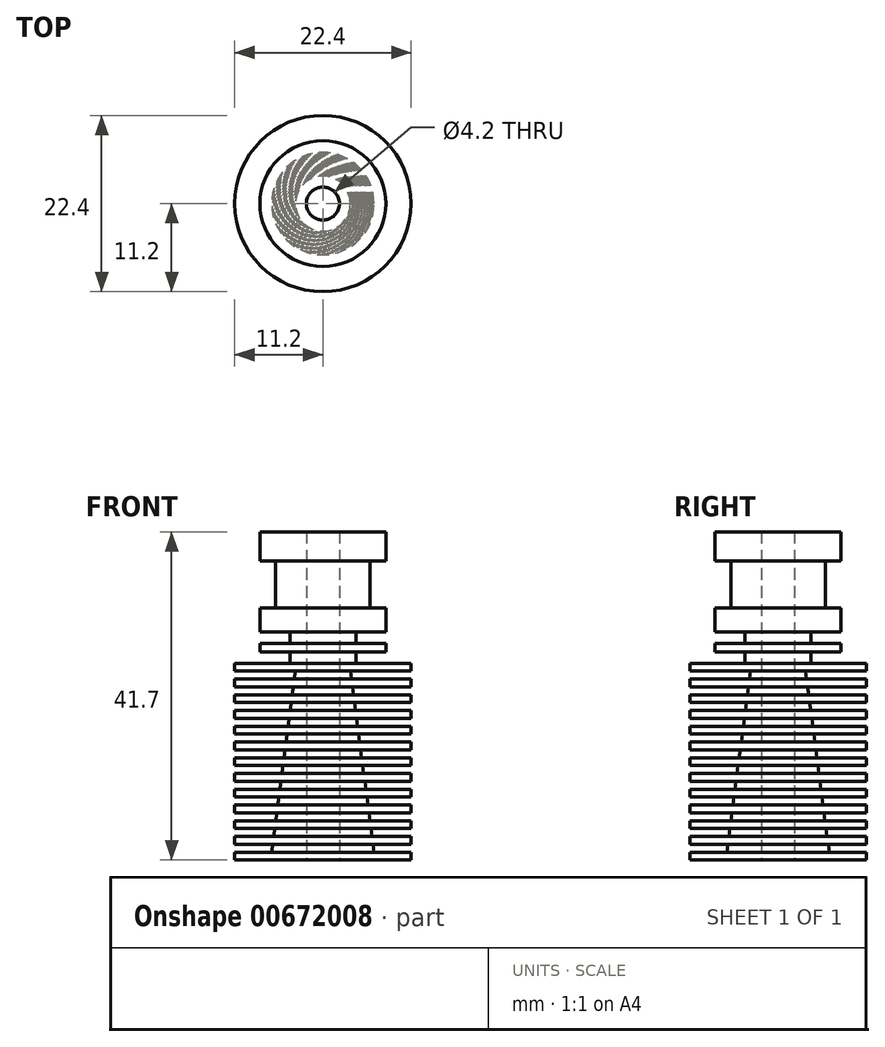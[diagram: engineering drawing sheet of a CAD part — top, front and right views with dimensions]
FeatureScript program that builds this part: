
annotation { "Feature Type Name" : "Feature", "Feature Type Description" : "" }
export const myFeature = defineFeature(function(context is Context, id is Id, definition is map)
    precondition{}
    {
        {
            var Q0;
            Q0=qCreatedBy(makeId("Front.planeOp"),FACE);
            var sketch = newSketch(context, id + "F0", { "sketchPlane" : qUnion([Q0])});
            skLineSegment(sketch, "E0", {"start": v(0, 0) * mm, "end": v(0, -46.74) * mm, "construction": true});
            skLineSegment(sketch, "E1", {"start": v(0, 0) * mm, "end": v(8, 0) * mm});
            skLineSegment(sketch, "E2", {"start": v(8, 0) * mm, "end": v(8, -3.7) * mm});
            skLineSegment(sketch, "E3", {"start": v(8, -3.7) * mm, "end": v(6, -3.7) * mm});
            skLineSegment(sketch, "E4", {"start": v(6, -3.7) * mm, "end": v(6, -9.7) * mm});
            skLineSegment(sketch, "E5", {"start": v(6, -9.7) * mm, "end": v(8, -9.7) * mm});
            skLineSegment(sketch, "E6", {"start": v(8, -9.7) * mm, "end": v(8, -12.7) * mm});
            skLineSegment(sketch, "E7", {"start": v(8, -12.7) * mm, "end": v(4.2, -12.7) * mm});
            skLineSegment(sketch, "E8", {"start": v(4.2, -12.7) * mm, "end": v(4.2, -14.15) * mm});
            skLineSegment(sketch, "E9", {"start": v(4.2, -14.15) * mm, "end": v(8, -14.15) * mm});
            skLineSegment(sketch, "E10", {"start": v(8, -14.15) * mm, "end": v(8, -15.24) * mm});
            skLineSegment(sketch, "E11", {"start": v(8, -15.24) * mm, "end": v(4.2, -15.24) * mm});
            skLineSegment(sketch, "E12", {"start": v(4.2, -15.24) * mm, "end": v(4.2, -16.7) * mm});
            skLineSegment(sketch, "E13", {"start": v(4.2, -16.7) * mm, "end": v(11.2, -16.7) * mm});
            skLineSegment(sketch, "E14", {"start": v(11.2, -16.7) * mm, "end": v(11.2, -41.7) * mm});
            skLineSegment(sketch, "E15", {"start": v(11.2, -41.7) * mm, "end": v(0, -41.7) * mm});
            skLineSegment(sketch, "E16", {"start": v(0, 0) * mm, "end": v(0, -41.7) * mm});
            skSolve(sketch);
        }
        {
            var Q0;
            Q0=makeQuery(id+"F0.imprint","IMPRINT",FACE,{"disambiguationData":[TD([[makeQuery(id+"F0.imprint","IMPRINT",EDGE,{"derivedFrom":sQuery(id+"F0.wireOp",EDGE,"E1")}),-1.0]])]});
            var Q1;
            Q1=sQuery(id+"F0.wireOp",EDGE,"E0");
            revolve(context, id + "F1", {"entities" : qUnion([Q0]), "axis" : qUnion([Q1]), "revolveType" : RevolveType.FULL});
        }
        {
            var Q0;
            Q0=makeQuery(id+"F1.opRevolve","SWEPT_FACE",FACE,{"disambiguationData":[OSD([sQuery(id+"F0.wireOp",EDGE,"E15")])]});
            var sketch = newSketch(context, id + "F2", { "sketchPlane" : qUnion([Q0])});
            skPoint(sketch, "E17", {"position": v(0, 0) * mm});
            skSolve(sketch);
        }
        {
            var Q0;
            Q0=sQuery(id+"F2.wireOp",VERTEX,"E17");
            var Q1;
            Q1=makeQuery(id+"F1.opRevolve","SWEPT_BODY",BODY,{"disambiguationData":[OSD([sQuery(id+"F0.wireOp",EDGE,"E1"),sQuery(id+"F0.wireOp",EDGE,"E2"),sQuery(id+"F0.wireOp",EDGE,"E3"),sQuery(id+"F0.wireOp",EDGE,"E4"),sQuery(id+"F0.wireOp",EDGE,"E5"),sQuery(id+"F0.wireOp",EDGE,"E6"),sQuery(id+"F0.wireOp",EDGE,"E7"),sQuery(id+"F0.wireOp",EDGE,"E8"),sQuery(id+"F0.wireOp",EDGE,"E9"),sQuery(id+"F0.wireOp",EDGE,"E10"),sQuery(id+"F0.wireOp",EDGE,"E11"),sQuery(id+"F0.wireOp",EDGE,"E12"),sQuery(id+"F0.wireOp",EDGE,"E13"),sQuery(id+"F0.wireOp",EDGE,"E14"),sQuery(id+"F0.wireOp",EDGE,"E15"),sQuery(id+"F0.wireOp",EDGE,"E16")])]});
            hole(context, id + "F3", {"style" : HoleStyle.SIMPLE, "endStyle" : HoleEndStyle.THROUGH, "standardTappedOrClearance" : lookupTablePath({ "standard" : "ISO", "engagement" : "75%", "pitch" : "0.8 mm", "size" : "M5", "type" : "Tapped" }), "standardBlindInLast" : lookupTablePath({ "standard" : "ISO", "engagement" : "75%", "pitch" : "0.8 mm", "size" : "M5", "type" : "Tapped" }), "holeDiameter" : 4.2 * mm, "majorDiameter" : 5 * mm, "showTappedDepth" : true, "isTappedThrough" : true, "tappedDepth" : 7.6 * mm, "tapClearance" : 3, "startFromSketch" : true, "locations" : qUnion([Q0]), "scope" : qUnion([Q1])});
        }
        {
            var Q0;
            Q0=qCreatedBy(makeId("Front.planeOp"),FACE);
            var sketch = newSketch(context, id + "F4", { "sketchPlane" : qUnion([Q0])});
            skLineSegment(sketch, "E18", {"start": v(0, -16.7) * mm, "end": v(11.2, -16.7) * mm});
            skLineSegment(sketch, "E19", {"start": v(11.2, -16.7) * mm, "end": v(11.2, -17.7) * mm});
            skLineSegment(sketch, "E20", {"start": v(11.2, -17.7) * mm, "end": v(3.5, -17.7) * mm});
            skLineSegment(sketch, "E21", {"start": v(3.63, -18.7) * mm, "end": v(11.2, -18.7) * mm});
            skLineSegment(sketch, "E22", {"start": v(11.2, -18.7) * mm, "end": v(11.2, -17.7) * mm});
            skLineSegment(sketch, "E23", {"start": v(0, -16.7) * mm, "end": v(0, -19.3) * mm});
            skLineSegment(sketch, "E24", {"start": v(11.2, -19.7) * mm, "end": v(3.76, -19.7) * mm});
            skLineSegment(sketch, "E25", {"start": v(3.9, -20.7) * mm, "end": v(11.2, -20.7) * mm});
            skLineSegment(sketch, "E26", {"start": v(11.2, -21.7) * mm, "end": v(4.02, -21.7) * mm});
            skLineSegment(sketch, "E27", {"start": v(4.15, -22.7) * mm, "end": v(11.2, -22.7) * mm});
            skLineSegment(sketch, "E28", {"start": v(11.2, -23.7) * mm, "end": v(4.28, -23.7) * mm});
            skLineSegment(sketch, "E29", {"start": v(4.41, -24.7) * mm, "end": v(11.2, -24.7) * mm});
            skLineSegment(sketch, "E30", {"start": v(11.2, -25.7) * mm, "end": v(4.54, -25.7) * mm});
            skLineSegment(sketch, "E31", {"start": v(4.67, -26.7) * mm, "end": v(11.2, -26.7) * mm});
            skLineSegment(sketch, "E32", {"start": v(11.2, -27.7) * mm, "end": v(4.8, -27.7) * mm});
            skLineSegment(sketch, "E33", {"start": v(4.93, -28.7) * mm, "end": v(11.2, -28.7) * mm});
            skLineSegment(sketch, "E34", {"start": v(11.2, -29.7) * mm, "end": v(5.07, -29.7) * mm});
            skLineSegment(sketch, "E35", {"start": v(5.2, -30.7) * mm, "end": v(11.2, -30.7) * mm});
            skLineSegment(sketch, "E36", {"start": v(11.2, -31.7) * mm, "end": v(5.33, -31.7) * mm});
            skLineSegment(sketch, "E37", {"start": v(5.46, -32.7) * mm, "end": v(11.2, -32.7) * mm});
            skLineSegment(sketch, "E38", {"start": v(11.2, -33.7) * mm, "end": v(5.59, -33.7) * mm});
            skLineSegment(sketch, "E39", {"start": v(5.72, -34.7) * mm, "end": v(11.2, -34.7) * mm});
            skLineSegment(sketch, "E40", {"start": v(11.2, -35.7) * mm, "end": v(5.85, -35.7) * mm});
            skLineSegment(sketch, "E41", {"start": v(5.98, -36.7) * mm, "end": v(11.2, -36.7) * mm});
            skLineSegment(sketch, "E42", {"start": v(11.2, -37.7) * mm, "end": v(6.1, -37.7) * mm});
            skLineSegment(sketch, "E43", {"start": v(6.24, -38.7) * mm, "end": v(11.2, -38.7) * mm});
            skLineSegment(sketch, "E44", {"start": v(11.2, -39.7) * mm, "end": v(6.37, -39.7) * mm});
            skLineSegment(sketch, "E45", {"start": v(6.5, -40.7) * mm, "end": v(11.2, -40.7) * mm});
            skLineSegment(sketch, "E46", {"start": v(11.2, -40.7) * mm, "end": v(11.2, -39.7) * mm});
            skLineSegment(sketch, "E47", {"start": v(11.2, -38.7) * mm, "end": v(11.2, -37.7) * mm});
            skLineSegment(sketch, "E48", {"start": v(11.2, -36.7) * mm, "end": v(11.2, -35.7) * mm});
            skLineSegment(sketch, "E49", {"start": v(11.2, -34.7) * mm, "end": v(11.2, -33.7) * mm});
            skLineSegment(sketch, "E50", {"start": v(11.2, -32.7) * mm, "end": v(11.2, -31.7) * mm});
            skLineSegment(sketch, "E51", {"start": v(11.2, -30.7) * mm, "end": v(11.2, -29.7) * mm});
            skLineSegment(sketch, "E52", {"start": v(11.2, -28.7) * mm, "end": v(11.2, -27.7) * mm});
            skLineSegment(sketch, "E53", {"start": v(11.2, -26.7) * mm, "end": v(11.2, -25.7) * mm});
            skLineSegment(sketch, "E54", {"start": v(11.2, -24.7) * mm, "end": v(11.2, -23.7) * mm});
            skLineSegment(sketch, "E55", {"start": v(11.2, -22.7) * mm, "end": v(11.2, -21.7) * mm});
            skLineSegment(sketch, "E56", {"start": v(11.2, -19.7) * mm, "end": v(11.2, -20.7) * mm});
            skLineSegment(sketch, "E57", {"start": v(3.5, -17.7) * mm, "end": v(6.5, -40.7) * mm});
            skPoint(sketch, "E58.orphan", {"position": v(3.5, -18.7) * mm});
            skPoint(sketch, "E59.orphan", {"position": v(3.5, -19.7) * mm});
            skSolve(sketch);
        }
        {
            var Q0;
            Q0 = qSketchRegion(id + "F4", true);
            var Q1;
            Q1=sQuery(id+"F4.wireOp",EDGE,"E23");
            revolve(context, id + "F5", {"operationType" : NewBodyOperationType.REMOVE, "entities" : qUnion([Q0]), "axis" : qUnion([Q1]), "revolveType" : RevolveType.FULL, "oppositeDirection" : true});
        }
    });
